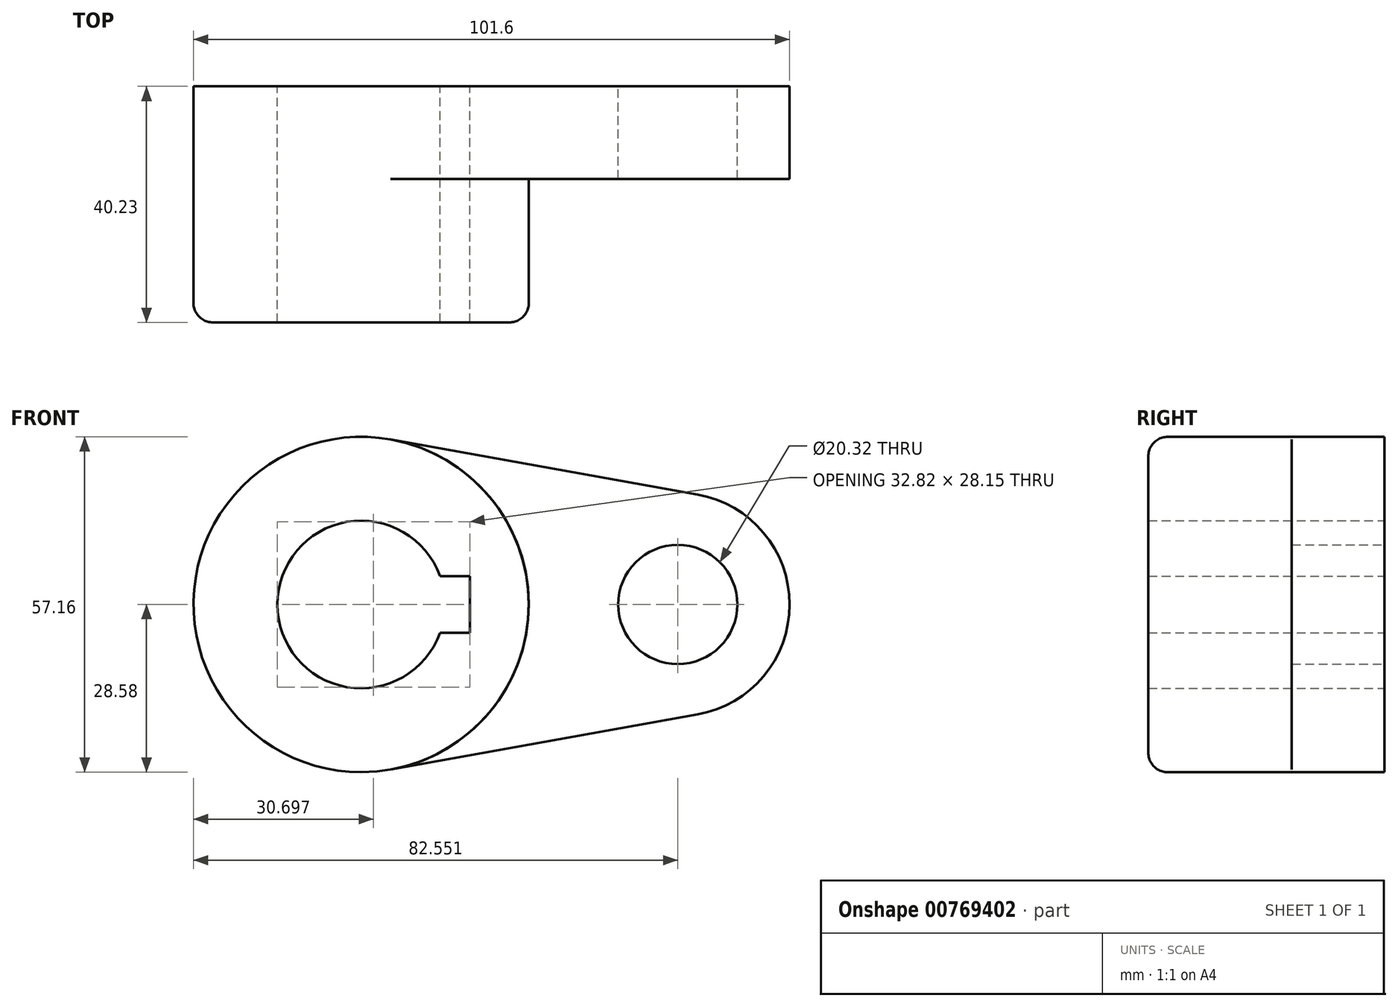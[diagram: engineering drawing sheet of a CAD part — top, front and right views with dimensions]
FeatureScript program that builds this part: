
annotation { "Feature Type Name" : "Feature", "Feature Type Description" : "" }
export const myFeature = defineFeature(function(context is Context, id is Id, definition is map)
    precondition{}
    {
        {
            var Q0;
            Q0=qCreatedBy(makeId("Front.planeOp"),FACE);
            var sketch = newSketch(context, id + "F0", { "sketchPlane" : qUnion([Q0])});
            skCircle(sketch, "E0", {"center": v(-12.83, 0) * mm, "radius": 14.29 * mm});
            skCircle(sketch, "E1", {"center": v(-12.83, 0) * mm, "radius": 28.58 * mm});
            skLineSegment(sketch, "E2", {"start": v(-12.83, 0) * mm, "end": v(41.14, 0) * mm, "construction": true});
            skCircle(sketch, "E3", {"center": v(41.14, 0) * mm, "radius": 10.16 * mm});
            skCircle(sketch, "E4", {"center": v(41.14, 0) * mm, "radius": 19.05 * mm});
            skLineSegment(sketch, "E5", {"start": v(0.61, 4.83) * mm, "end": v(5.7, 4.83) * mm});
            skLineSegment(sketch, "E6", {"start": v(5.7, 4.83) * mm, "end": v(5.7, -4.83) * mm});
            skLineSegment(sketch, "E7", {"start": v(5.7, -4.83) * mm, "end": v(0.61, -4.83) * mm});
            skLineSegment(sketch, "E8", {"start": v(-7.8, 28.13) * mm, "end": v(44.5, 18.75) * mm});
            skLineSegment(sketch, "E9", {"start": v(44.5, -18.75) * mm, "end": v(-7.8, -28.13) * mm});
            skSolve(sketch);
        }
        {
            var Q0;
            {var subQ3=sQuery(id+"F0.wireOp",EDGE,"E5");Q0=makeQuery(id+"F0.imprint","IMPRINT",FACE,{"disambiguationData":[TD([[makeQuery(id+"F0.imprint","IMPRINT",EDGE,{"derivedFrom":subQ3}),1.0]])]});}
            extrude(context, id + "F1", {"entities" : qUnion([Q0]), "depth" : 40.23 * mm, "offsetDistance" : 25.4 * mm});
        }
        {
            var Q0;
            Q0 = qSketchRegion(id + "F0", true);
            extrude(context, id + "F2", {"entities" : qUnion([Q0]), "operationType" : NewBodyOperationType.ADD, "depth" : 15.77 * mm, "offsetDistance" : 25.4 * mm});
        }
        {
            var Q0;
            Q0=makeQuery(id+"F1.opExtrude","CAP_EDGE",EDGE,{"disambiguationData":[OSD([sQuery(id+"F0.wireOp",EDGE,"E1")])],"isStart":false});
            fillet(context, id + "F3", {"entities" : qUnion([Q0]), "radius" : 3.3 * mm, "tangentPropagation" : true, "allowEdgeOverflow" : false});
        }
    });
